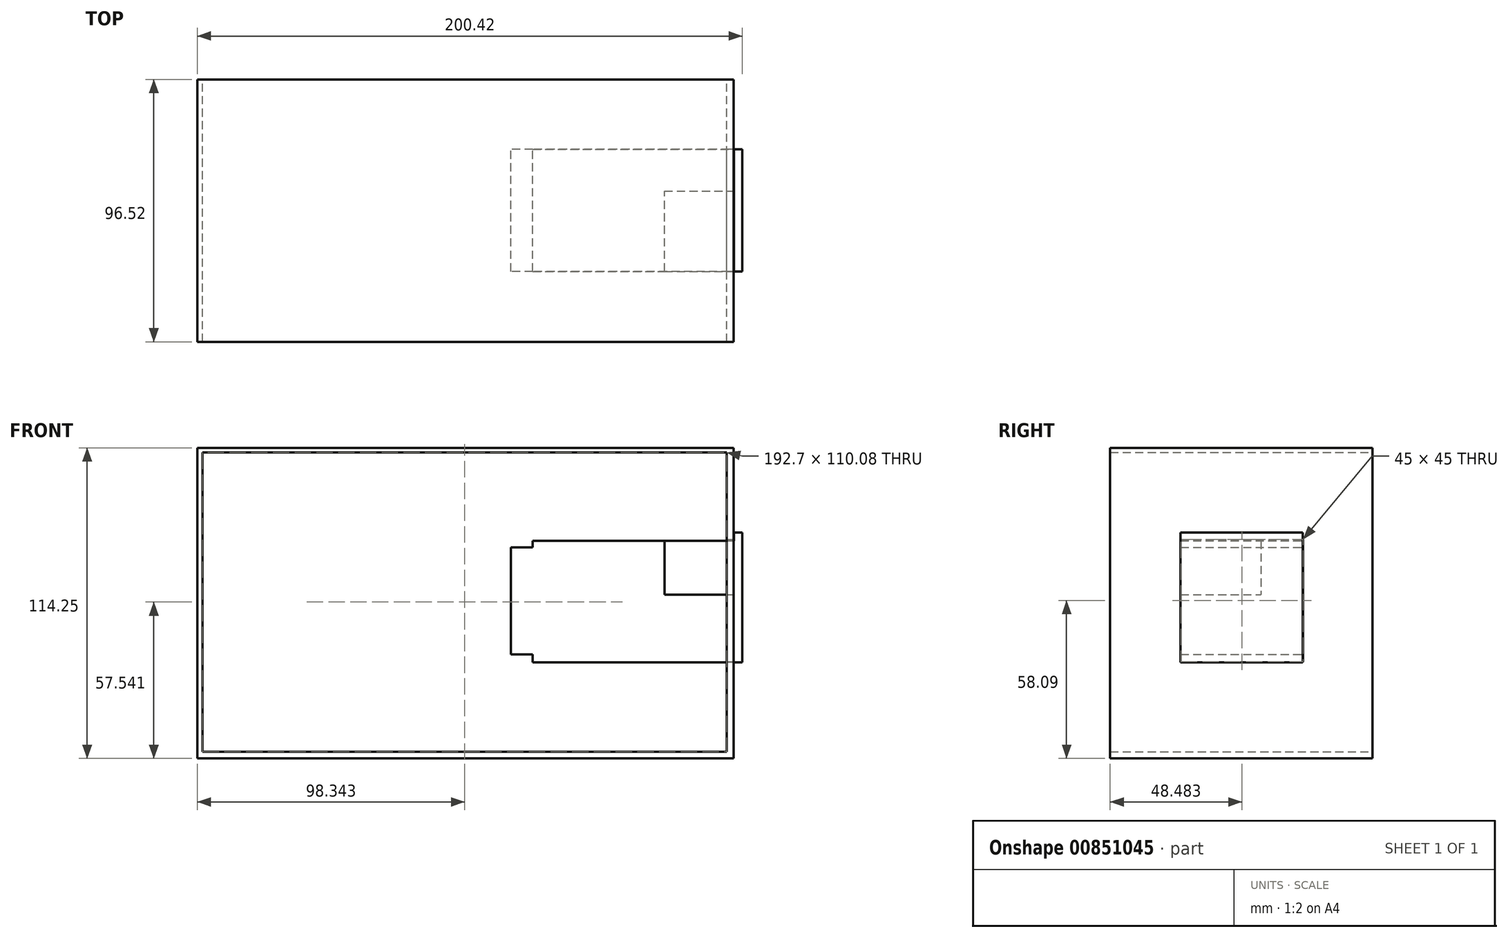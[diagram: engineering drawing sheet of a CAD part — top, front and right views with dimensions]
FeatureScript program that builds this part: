
annotation { "Feature Type Name" : "Feature", "Feature Type Description" : "" }
export const myFeature = defineFeature(function(context is Context, id is Id, definition is map)
    precondition{}
    {
        {
            var Q0;
            Q0=qCreatedBy(makeId("Front.planeOp"),FACE);
            var sketch = newSketch(context, id + "F0", { "sketchPlane" : qUnion([Q0])});
            skLineSegment(sketch, "E0.bottom", {"start": v(-51.51, 9.2) * mm, "end": v(22.49, 9.2) * mm});
            skLineSegment(sketch, "E0.top", {"start": v(-51.51, -35.5) * mm, "end": v(22.49, -35.5) * mm});
            skLineSegment(sketch, "E0.left", {"start": v(-51.51, 9.2) * mm, "end": v(-51.51, -35.5) * mm});
            skLineSegment(sketch, "E0.right", {"start": v(22.49, 9.2) * mm, "end": v(22.49, -35.5) * mm});
            skLineSegment(sketch, "E1.bottom", {"start": v(-51.51, 6.77) * mm, "end": v(-59.51, 6.77) * mm});
            skLineSegment(sketch, "E1.top", {"start": v(-51.51, -32.6) * mm, "end": v(-59.51, -32.6) * mm});
            skLineSegment(sketch, "E1.left", {"start": v(-51.51, 6.77) * mm, "end": v(-51.51, -32.6) * mm});
            skLineSegment(sketch, "E1.right", {"start": v(-59.51, 6.77) * mm, "end": v(-59.51, -32.6) * mm});
            skLineSegment(sketch, "E2.bottom", {"start": v(25.53, -35.5) * mm, "end": v(22.49, -35.5) * mm});
            skLineSegment(sketch, "E2.top", {"start": v(25.53, 12.24) * mm, "end": v(22.49, 12.24) * mm});
            skLineSegment(sketch, "E2.left", {"start": v(25.53, -35.5) * mm, "end": v(25.53, 12.24) * mm});
            skLineSegment(sketch, "E2.right", {"start": v(22.49, -35.5) * mm, "end": v(22.49, 12.24) * mm});
            skSolve(sketch);
        }
        {
            var Q0;
            {var subQ3=sQuery(id+"F0.wireOp",EDGE,"E0.bottom");Q0=makeQuery(id+"F0.imprint","IMPRINT",FACE,{"disambiguationData":[TD([[makeQuery(id+"F0.imprint","IMPRINT",EDGE,{"derivedFrom":subQ3}),-1.0]])]});}
            var Q1;
            Q1=makeQuery(id+"F0.imprint","IMPRINT",FACE,{"disambiguationData":[TD([[makeQuery(id+"F0.imprint","IMPRINT",EDGE,{"derivedFrom":sQuery(id+"F0.wireOp",EDGE,"E1.bottom")}),1.0]])]});
            var Q2;
            {var subQ2=sQuery(id+"F0.wireOp",EDGE,"E2.bottom");Q2=makeQuery(id+"F0.imprint","IMPRINT",FACE,{"disambiguationData":[TD([[makeQuery(id+"F0.imprint","IMPRINT",EDGE,{"derivedFrom":subQ2}),-1.0]])]});}
            extrude(context, id + "F1", {"entities" : qUnion([Q0, Q1, Q2]), "depth" : 45 * mm, "offsetDistance" : 25.4 * mm});
        }
        {
            var Q0;
            Q0=qCreatedBy(makeId("Front.planeOp"),FACE);
            var sketch = newSketch(context, id + "F2", { "sketchPlane" : qUnion([Q0])});
            skLineSegment(sketch, "E3.bottom", {"start": v(-177.94, 32.67) * mm, "end": v(22.06, 32.67) * mm});
            skLineSegment(sketch, "E3.top", {"start": v(-177.94, -57.33) * mm, "end": v(22.06, -57.33) * mm});
            skLineSegment(sketch, "E3.left", {"start": v(-177.94, 32.67) * mm, "end": v(-177.94, -57.33) * mm});
            skLineSegment(sketch, "E3.right", {"start": v(22.06, 32.67) * mm, "end": v(22.06, -57.33) * mm});
            skLineSegment(sketch, "E4.bottom", {"start": v(20.26, 30.6) * mm, "end": v(-175.91, 30.6) * mm});
            skLineSegment(sketch, "E4.top", {"start": v(20.26, -55.36) * mm, "end": v(-175.91, -55.36) * mm});
            skLineSegment(sketch, "E4.left", {"start": v(20.26, 30.6) * mm, "end": v(20.26, -55.36) * mm});
            skLineSegment(sketch, "E4.right", {"start": v(-175.91, 30.6) * mm, "end": v(-175.91, -55.36) * mm});
            skSolve(sketch);
        }
        {
            var Q0;
            Q0 = qSketchRegion(id + "F2", true);
            extrude(context, id + "F3", {"entities" : qUnion([Q0]), "operationType" : NewBodyOperationType.ADD, "depth" : 120 * mm, "offsetDistance" : 25.4 * mm});
        }
        {
            var Q0;
            Q0=makeQuery(id+"F1.opExtrude","SWEPT_BODY",BODY,{"disambiguationData":[OSD([sQuery(id+"F0.wireOp",EDGE,"E0.bottom"),sQuery(id+"F0.wireOp",EDGE,"E0.top"),sQuery(id+"F0.wireOp",EDGE,"E0.left"),sQuery(id+"F0.wireOp",EDGE,"E1.bottom"),sQuery(id+"F0.wireOp",EDGE,"E1.top"),sQuery(id+"F0.wireOp",EDGE,"E1.right"),sQuery(id+"F0.wireOp",EDGE,"E2.bottom"),sQuery(id+"F0.wireOp",EDGE,"E2.top"),sQuery(id+"F0.wireOp",EDGE,"E2.left"),sQuery(id+"F0.wireOp",EDGE,"E2.right")])]});
            transform(context, id + "F4", {"entities" : qUnion([Q0]), "transformType" : TransformType.TRANSLATION_3D, "dx" : 0 * mm, "dy" : 20.57 * mm, "dz" : 0 * mm, "makeCopy" : false});
        }
        {
            var Q0;
            Q0 = qSketchRegion(id + "F0", true);
            extrude(context, id + "F5", {"entities" : qUnion([Q0]), "depth" : 44.96 * mm, "offsetDistance" : 25.4 * mm});
        }
        {
            var Q0;
            Q0=makeQuery(id+"F1.opExtrude","SWEPT_BODY",BODY,{"disambiguationData":[OSD([sQuery(id+"F0.wireOp",EDGE,"E0.bottom"),sQuery(id+"F0.wireOp",EDGE,"E0.top"),sQuery(id+"F0.wireOp",EDGE,"E0.left"),sQuery(id+"F0.wireOp",EDGE,"E1.bottom"),sQuery(id+"F0.wireOp",EDGE,"E1.top"),sQuery(id+"F0.wireOp",EDGE,"E1.right"),sQuery(id+"F0.wireOp",EDGE,"E2.bottom"),sQuery(id+"F0.wireOp",EDGE,"E2.top"),sQuery(id+"F0.wireOp",EDGE,"E2.left"),sQuery(id+"F0.wireOp",EDGE,"E2.right")])]});
            deleteBodies(context, id + "F6", {"entities" : qUnion([Q0])});
        }
        {
            var Q0;
            Q0=qCreatedBy(makeId("Front.planeOp"),FACE);
            var sketch = newSketch(context, id + "F7", { "sketchPlane" : qUnion([Q0])});
            skLineSegment(sketch, "E5.bottom", {"start": v(-174.9, 68.07) * mm, "end": v(22.3, 68.07) * mm});
            skLineSegment(sketch, "E5.top", {"start": v(-174.9, -46.18) * mm, "end": v(22.3, -46.18) * mm});
            skLineSegment(sketch, "E5.left", {"start": v(-174.9, 68.07) * mm, "end": v(-174.9, -46.18) * mm});
            skLineSegment(sketch, "E5.right", {"start": v(22.3, 68.07) * mm, "end": v(22.3, -46.18) * mm});
            skLineSegment(sketch, "E6.bottom", {"start": v(-172.9, 66.4) * mm, "end": v(19.8, 66.4) * mm});
            skLineSegment(sketch, "E6.top", {"start": v(-172.9, -43.68) * mm, "end": v(19.8, -43.68) * mm});
            skLineSegment(sketch, "E6.left", {"start": v(-172.9, 66.4) * mm, "end": v(-172.9, -43.68) * mm});
            skLineSegment(sketch, "E6.right", {"start": v(19.8, 66.4) * mm, "end": v(19.8, -43.68) * mm});
            skSolve(sketch);
        }
        {
            var Q0;
            Q0 = qSketchRegion(id + "F7", true);
            extrude(context, id + "F8", {"entities" : qUnion([Q0]), "depth" : 96.52 * mm, "offsetDistance" : 25.4 * mm});
        }
        {
            var Q0;
            Q0=makeQuery(id+"F8.opExtrude","SWEPT_BODY",BODY,{"disambiguationData":[OSD([sQuery(id+"F7.wireOp",EDGE,"E5.bottom"),sQuery(id+"F7.wireOp",EDGE,"E5.top"),sQuery(id+"F7.wireOp",EDGE,"E5.left"),sQuery(id+"F7.wireOp",EDGE,"E5.right"),sQuery(id+"F7.wireOp",EDGE,"E6.bottom"),sQuery(id+"F7.wireOp",EDGE,"E6.top"),sQuery(id+"F7.wireOp",EDGE,"E6.left"),sQuery(id+"F7.wireOp",EDGE,"E6.right")])]});
            transform(context, id + "F9", {"entities" : qUnion([Q0]), "transformType" : TransformType.TRANSLATION_3D, "dx" : 0 * mm, "dy" : 10.16 * mm, "dz" : 0 * mm, "makeCopy" : false});
        }
        {
            var Q0;
            Q0=makeQuery(id+"F8.opExtrude","SWEPT_FACE",FACE,{"disambiguationData":[OSD([sQuery(id+"F7.wireOp",EDGE,"E5.right")])]});
            var sketch = newSketch(context, id + "F10", { "sketchPlane" : qUnion([Q0])});
            skLineSegment(sketch, "E7.bottom", {"start": v(-60.38, 34.41) * mm, "end": v(-15.38, 34.41) * mm});
            skLineSegment(sketch, "E7.top", {"start": v(-60.38, -10.59) * mm, "end": v(-15.38, -10.59) * mm});
            skLineSegment(sketch, "E7.left", {"start": v(-60.38, 34.41) * mm, "end": v(-60.38, -10.59) * mm});
            skLineSegment(sketch, "E7.right", {"start": v(-15.38, 34.41) * mm, "end": v(-15.38, -10.59) * mm});
            skSolve(sketch);
        }
        {
            var Q0;
            Q0 = qSketchRegion(id + "F10", true);
            extrude(context, id + "F11", {"entities" : qUnion([Q0]), "operationType" : NewBodyOperationType.REMOVE, "oppositeDirection" : true, "depth" : 25.4 * mm, "offsetDistance" : 25.4 * mm});
        }
        {
            var Q0;
            Q0=makeQuery(id+"F5.opExtrude","SWEPT_BODY",BODY,{"disambiguationData":[OSD([sQuery(id+"F0.wireOp",EDGE,"E0.bottom"),sQuery(id+"F0.wireOp",EDGE,"E0.top"),sQuery(id+"F0.wireOp",EDGE,"E0.left"),sQuery(id+"F0.wireOp",EDGE,"E1.bottom"),sQuery(id+"F0.wireOp",EDGE,"E1.top"),sQuery(id+"F0.wireOp",EDGE,"E1.right"),sQuery(id+"F0.wireOp",EDGE,"E2.bottom"),sQuery(id+"F0.wireOp",EDGE,"E2.top"),sQuery(id+"F0.wireOp",EDGE,"E2.left"),sQuery(id+"F0.wireOp",EDGE,"E2.right")])]});
            transform(context, id + "F12", {"entities" : qUnion([Q0]), "transformType" : TransformType.TRANSLATION_3D, "dx" : 0 * mm, "dy" : -15.5 * mm, "dz" : 24.64 * mm, "makeCopy" : false});
        }
    });
